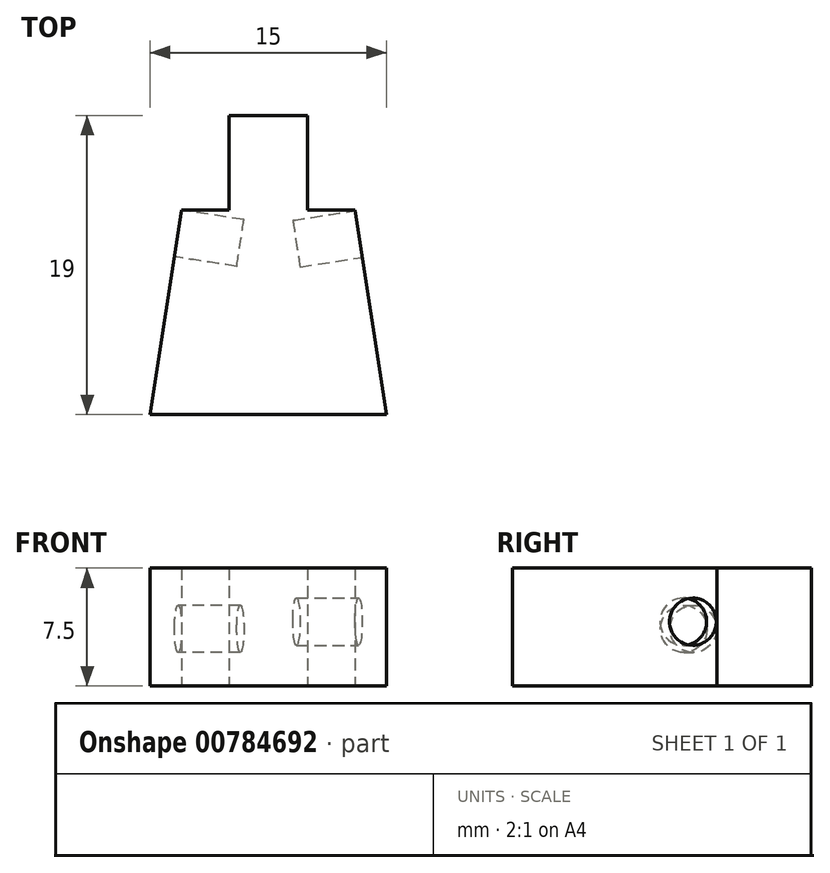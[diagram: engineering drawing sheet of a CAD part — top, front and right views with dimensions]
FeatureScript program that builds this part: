
annotation { "Feature Type Name" : "Feature", "Feature Type Description" : "" }
export const myFeature = defineFeature(function(context is Context, id is Id, definition is map)
    precondition{}
    {
        {
            var Q0;
            Q0=qCreatedBy(makeId("Top.planeOp"),FACE);
            var sketch = newSketch(context, id + "F0", { "sketchPlane" : qUnion([Q0])});
            skPoint(sketch, "E0.start.orphan", {"position": v(0, 19) * mm});
            skPoint(sketch, "E1.start.orphan", {"position": v(0, 6.93) * mm});
            skLineSegment(sketch, "E2", {"start": v(0, 0) * mm, "end": v(15, 0) * mm});
            skLineSegment(sketch, "E3", {"start": v(0, 0) * mm, "end": v(2, 13) * mm});
            skLineSegment(sketch, "E4", {"start": v(15, 0) * mm, "end": v(13, 13) * mm});
            skLineSegment(sketch, "E5", {"start": v(2, 13) * mm, "end": v(13, 13) * mm});
            skLineSegment(sketch, "E6", {"start": v(5, 19) * mm, "end": v(10, 19) * mm});
            skLineSegment(sketch, "E7", {"start": v(5, 19) * mm, "end": v(5, 13) * mm});
            skLineSegment(sketch, "E8", {"start": v(5, 13) * mm, "end": v(10, 13) * mm});
            skLineSegment(sketch, "E9", {"start": v(10, 13) * mm, "end": v(10, 19) * mm});
            skSolve(sketch);
        }
        {
            var Q0;
            Q0=makeQuery(id+"F0.imprint","IMPRINT",FACE,{"disambiguationData":[TD([[makeQuery(id+"F0.imprint","IMPRINT",EDGE,{"derivedFrom":sQuery(id+"F0.wireOp",EDGE,"E6")}),-1.0]])]});
            var Q1;
            Q1=makeQuery(id+"F0.imprint","IMPRINT",FACE,{"disambiguationData":[TD([[makeQuery(id+"F0.imprint","IMPRINT",EDGE,{"derivedFrom":sQuery(id+"F0.wireOp",EDGE,"E2")}),1.0]])]});
            extrude(context, id + "F1", {"entities" : qUnion([Q0, Q1]), "depth" : 7.5 * mm, "offsetDistance" : 25 * mm});
        }
        {
            var Q0;
            Q0=makeQuery(id+"F1.opExtrude","SWEPT_FACE",FACE,{"disambiguationData":[OSD([sQuery(id+"F0.wireOp",EDGE,"E4")])]});
            var sketch = newSketch(context, id + "F2", { "sketchPlane" : qUnion([Q0])});
            skCircle(sketch, "E10", {"center": v(9.32, 4.1) * mm, "radius": 1.5 * mm});
            skSolve(sketch);
        }
        {
            var Q0;
            Q0=makeQuery(id+"F2.imprint","IMPRINT",FACE,{"disambiguationData":[TD([[makeQuery(id+"F2.imprint","IMPRINT",EDGE,{"derivedFrom":sQuery(id+"F2.wireOp",EDGE,"E10")}),1.0]])]});
            extrude(context, id + "F3", {"entities" : qUnion([Q0]), "operationType" : NewBodyOperationType.REMOVE, "oppositeDirection" : true, "depth" : 4 * mm, "offsetDistance" : 25 * mm});
        }
        {
            var Q0;
            Q0=makeQuery(id+"F1.opExtrude","SWEPT_FACE",FACE,{"disambiguationData":[OSD([sQuery(id+"F0.wireOp",EDGE,"E3")])]});
            var sketch = newSketch(context, id + "F4", { "sketchPlane" : qUnion([Q0])});
            skCircle(sketch, "E11", {"center": v(-11.63, 3.64) * mm, "radius": 1.5 * mm});
            skSolve(sketch);
        }
        {
            var Q0;
            Q0=makeQuery(id+"F4.imprint","IMPRINT",FACE,{"disambiguationData":[TD([[makeQuery(id+"F4.imprint","IMPRINT",EDGE,{"derivedFrom":sQuery(id+"F4.wireOp",EDGE,"E11")}),1.0]])]});
            extrude(context, id + "F5", {"entities" : qUnion([Q0]), "operationType" : NewBodyOperationType.REMOVE, "oppositeDirection" : true, "depth" : 4 * mm, "offsetDistance" : 25 * mm});
        }
    });
